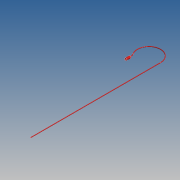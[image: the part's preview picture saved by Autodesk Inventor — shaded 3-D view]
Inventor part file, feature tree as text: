
AUTODESK INVENTOR PART (.ipt)
format: ipt  version: 2017 (Build 210142000, 142)  size: 211,968 bytes
history: native  units: mm
features: sketch x3, revolve x1, sweep x1
ambient origin geometry x8: Origin, YZ Plane, XZ Plane, XY Plane, X Axis, Y Axis, Z Axis, Center Point
bodies: Solid1 (feature_tree)
feature tree (5):
  revolve  "Revolution1"  [1 undecoded]
  sweep  "Sweep1"
  sketch  "Sketch1"  dims[d0=5.0mm d1=12.0mm]
  sketch  "Sketch2"  dims[d2=5.0mm d3=25.0mm]
  sketch  "Sketch3"  dims[d4=90.0deg d5=30.0mm d6=3.5mm d7=0.0mm d8=0.0mm d9=5.0mm d10=60.5mm d11=80.0mm d12=600.0mm]
note: 1 required parameter value undecoded (feature->parameter linkage not recoverable at this tier; creation-order binding heuristic only, values carry confidence <= 0.55)
